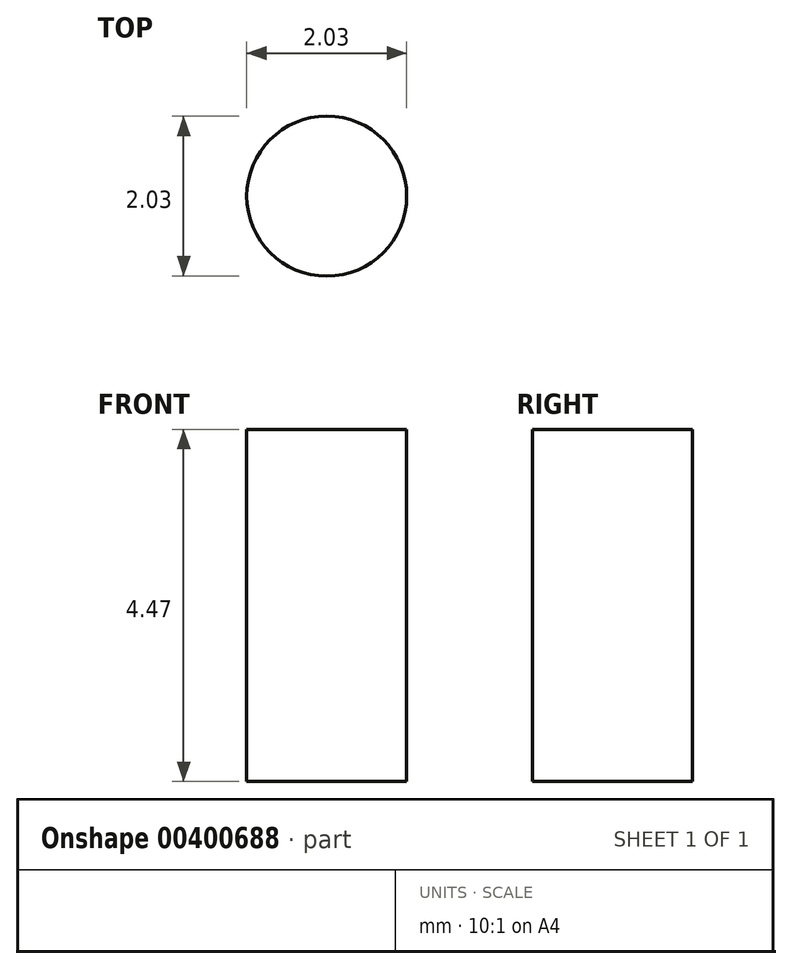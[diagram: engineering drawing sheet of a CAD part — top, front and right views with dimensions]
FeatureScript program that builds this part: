
annotation { "Feature Type Name" : "Feature", "Feature Type Description" : "" }
export const myFeature = defineFeature(function(context is Context, id is Id, definition is map)
    precondition{}
    {
        {
            var Q0;
            Q0=qCreatedBy(makeId("Top.planeOp"),FACE);
            var sketch = newSketch(context, id + "F0", { "sketchPlane" : qUnion([Q0])});
            skCircle(sketch, "E0", {"center": v(-54.44, 36.23) * mm, "radius": 1.02 * mm});
            skSolve(sketch);
        }
        {
            var Q0;
            Q0=makeQuery(id+"F0.imprint","IMPRINT",FACE,{"disambiguationData":[TD([[makeQuery(id+"F0.imprint","IMPRINT",EDGE,{"derivedFrom":sQuery(id+"F0.wireOp",EDGE,"E0")}),1.0]])]});
            extrude(context, id + "F1", {"entities" : qUnion([Q0]), "depth" : 4.47 * mm});
        }
    });
